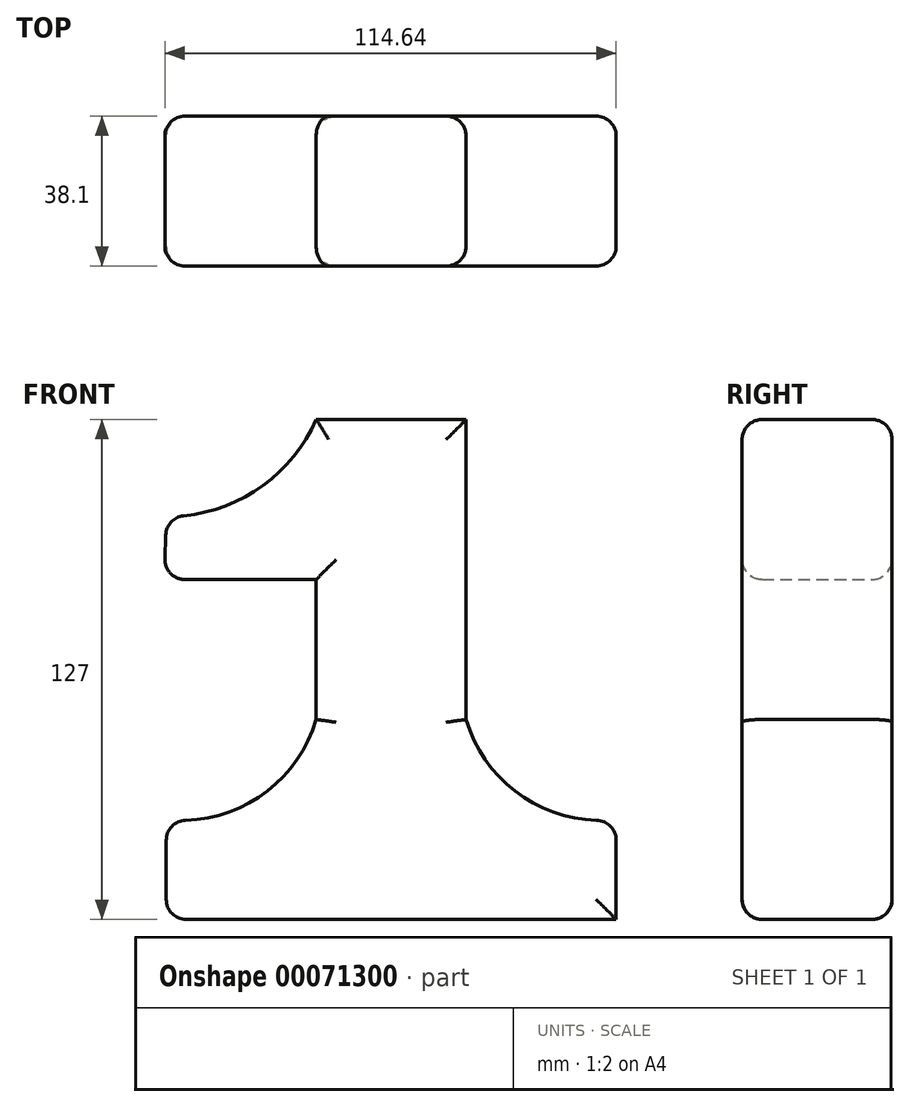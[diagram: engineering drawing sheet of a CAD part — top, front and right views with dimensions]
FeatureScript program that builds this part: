
annotation { "Feature Type Name" : "Feature", "Feature Type Description" : "" }
export const myFeature = defineFeature(function(context is Context, id is Id, definition is map)
    precondition{}
    {
        {
            var Q0;
            Q0=qCreatedBy(makeId("Front.planeOp"),FACE);
            var sketch = newSketch(context, id + "F0", { "sketchPlane" : qUnion([Q0])});
            skLineSegment(sketch, "E0.rect.bottom", {"start": v(19.05, -63.5) * mm, "end": v(-19.05, -63.5) * mm});
            skLineSegment(sketch, "E0.rect.top", {"start": v(19.05, 63.5) * mm, "end": v(-19.05, 63.5) * mm});
            skLineSegment(sketch, "E0.rect.left", {"start": v(19.05, -63.5) * mm, "end": v(19.05, 63.5) * mm});
            skLineSegment(sketch, "E0.rect.right", {"start": v(-19.05, -63.5) * mm, "end": v(-19.05, 63.5) * mm});
            skPoint(sketch, "E0.rect.middle", {"position": v(0, 0) * mm});
            skPoint(sketch, "E1", {"position": v(0, -63.5) * mm});
            skLineSegment(sketch, "E2", {"start": v(19.05, -63.5) * mm, "end": v(57.15, -63.5) * mm});
            skLineSegment(sketch, "E3", {"start": v(-19.05, -63.5) * mm, "end": v(-57.15, -63.5) * mm});
            skLineSegment(sketch, "E4", {"start": v(-57.15, -63.5) * mm, "end": v(-57.15, -38.1) * mm});
            skLineSegment(sketch, "E5", {"start": v(57.15, -63.5) * mm, "end": v(57.15, -38.1) * mm});
            skArc(sketch, "E6", {"start": v(-57.15, -38.1) * mm, "mid": v(-33.47, -32.35) * mm, "end": v(-19.05, -12.7) * mm});
            skArc(sketch, "E7", {"start": v(19.05, -12.7) * mm, "mid": v(33.47, -32.35) * mm, "end": v(57.15, -38.1) * mm});
            skArc(sketch, "E8", {"start": v(-57.15, 38.82) * mm, "mid": v(-34.41, 45.47) * mm, "end": v(-19.05, 63.5) * mm});
            skLineSegment(sketch, "E9", {"start": v(-19.05, 22.86) * mm, "end": v(-57.65, 22.86) * mm});
            skLineSegment(sketch, "E10", {"start": v(-57.65, 22.86) * mm, "end": v(-57.15, 38.82) * mm});
            skSolve(sketch);
        }
        {
            var Q0;
            {var subQ3=sQuery(id+"F0.wireOp",EDGE,"E0.rect.bottom");Q0=makeQuery(id+"F0.imprint","IMPRINT",FACE,{"disambiguationData":[TD([[makeQuery(id+"F0.imprint","IMPRINT",EDGE,{"derivedFrom":subQ3}),-1.0]])]});}
            var Q1;
            {var subQ0=sQuery(id+"F0.wireOp",EDGE,"E8");Q1=makeQuery(id+"F0.imprint","IMPRINT",FACE,{"disambiguationData":[TD([[makeQuery(id+"F0.imprint","IMPRINT",EDGE,{"derivedFrom":subQ0}),-1.0]])]});}
            var Q2;
            {var subQ0=sQuery(id+"F0.wireOp",EDGE,"E2");Q2=makeQuery(id+"F0.imprint","IMPRINT",FACE,{"disambiguationData":[TD([[makeQuery(id+"F0.imprint","IMPRINT",EDGE,{"derivedFrom":subQ0}),1.0]])]});}
            var Q3;
            {var subQ0=sQuery(id+"F0.wireOp",EDGE,"E3");Q3=makeQuery(id+"F0.imprint","IMPRINT",FACE,{"disambiguationData":[TD([[makeQuery(id+"F0.imprint","IMPRINT",EDGE,{"derivedFrom":subQ0}),-1.0]])]});}
            extrude(context, id + "F1", {"entities" : qUnion([Q0, Q1, Q2, Q3]), "endBound" : BoundingType.SYMMETRIC, "depth" : 38.1 * mm});
        }
        {
            var Q0;
            Q0=makeQuery(id+"F1.opExtrude","CAP_EDGE",EDGE,{"disambiguationData":[OSD([sQuery(id+"F0.wireOp",EDGE,"E0.rect.left")])],"isStart":false});
            var Q1;
            Q1=makeQuery(id+"F1.opExtrude","CAP_EDGE",EDGE,{"disambiguationData":[OSD([sQuery(id+"F0.wireOp",EDGE,"E7")])],"isStart":false});
            var Q2;
            Q2=makeQuery(id+"F1.opExtrude","CAP_EDGE",EDGE,{"disambiguationData":[OSD([sQuery(id+"F0.wireOp",EDGE,"E7")])],"isStart":true});
            var Q3;
            Q3=makeQuery(id+"F1.opExtrude","CAP_EDGE",EDGE,{"disambiguationData":[OSD([sQuery(id+"F0.wireOp",EDGE,"E0.rect.left")])],"isStart":true});
            var Q4;
            Q4=makeQuery(id+"F1.opExtrude","SWEPT_EDGE",EDGE,{"disambiguationData":[OSD([sQuery(id+"F0.wireOp",EDGE,"E5"),sQuery(id+"F0.wireOp",EDGE,"E7")])]});
            var Q5;
            Q5=makeQuery(id+"F1.opExtrude","CAP_EDGE",EDGE,{"disambiguationData":[OSD([sQuery(id+"F0.wireOp",EDGE,"E0.rect.top")])],"isStart":false});
            var Q6;
            Q6=makeQuery(id+"F1.opExtrude","CAP_EDGE",EDGE,{"disambiguationData":[OSD([sQuery(id+"F0.wireOp",EDGE,"E0.rect.top")])],"isStart":true});
            var Q7;
            Q7=makeQuery(id+"F1.opExtrude","CAP_EDGE",EDGE,{"disambiguationData":[OSD([sQuery(id+"F0.wireOp",EDGE,"E8")])],"isStart":false});
            var Q8;
            Q8=makeQuery(id+"F1.opExtrude","CAP_EDGE",EDGE,{"disambiguationData":[OSD([sQuery(id+"F0.wireOp",EDGE,"E8")])],"isStart":true});
            var Q9;
            Q9=makeQuery(id+"F1.opExtrude","CAP_EDGE",EDGE,{"disambiguationData":[OSD([sQuery(id+"F0.wireOp",EDGE,"E0.rect.right")])],"isStart":true});
            var Q10;
            Q10=makeQuery(id+"F1.opExtrude","CAP_EDGE",EDGE,{"disambiguationData":[OSD([sQuery(id+"F0.wireOp",EDGE,"E6")])],"isStart":true});
            var Q11;
            Q11=makeQuery(id+"F1.opExtrude","CAP_EDGE",EDGE,{"disambiguationData":[OSD([sQuery(id+"F0.wireOp",EDGE,"E9")])],"isStart":true});
            var Q12;
            Q12=makeQuery(id+"F1.opExtrude","CAP_EDGE",EDGE,{"disambiguationData":[OSD([sQuery(id+"F0.wireOp",EDGE,"E9")])],"isStart":false});
            var Q13;
            Q13=makeQuery(id+"F1.opExtrude","CAP_EDGE",EDGE,{"disambiguationData":[OSD([sQuery(id+"F0.wireOp",EDGE,"E0.rect.right")])],"isStart":false});
            var Q14;
            Q14=makeQuery(id+"F1.opExtrude","CAP_EDGE",EDGE,{"disambiguationData":[OSD([sQuery(id+"F0.wireOp",EDGE,"E6")])],"isStart":false});
            var Q15;
            Q15=makeQuery(id+"F1.opExtrude","CAP_EDGE",EDGE,{"disambiguationData":[OSD([sQuery(id+"F0.wireOp",EDGE,"E0.rect.bottom"),sQuery(id+"F0.wireOp",EDGE,"E2"),sQuery(id+"F0.wireOp",EDGE,"E3")])],"isStart":false});
            var Q16;
            Q16=makeQuery(id+"F1.opExtrude","CAP_EDGE",EDGE,{"disambiguationData":[OSD([sQuery(id+"F0.wireOp",EDGE,"E4")])],"isStart":false});
            var Q17;
            Q17=makeQuery(id+"F1.opExtrude","CAP_EDGE",EDGE,{"disambiguationData":[OSD([sQuery(id+"F0.wireOp",EDGE,"E5")])],"isStart":false});
            var Q18;
            Q18=makeQuery(id+"F1.opExtrude","CAP_EDGE",EDGE,{"disambiguationData":[OSD([sQuery(id+"F0.wireOp",EDGE,"E4")])],"isStart":true});
            var Q19;
            Q19=makeQuery(id+"F1.opExtrude","CAP_EDGE",EDGE,{"disambiguationData":[OSD([sQuery(id+"F0.wireOp",EDGE,"E0.rect.bottom"),sQuery(id+"F0.wireOp",EDGE,"E2"),sQuery(id+"F0.wireOp",EDGE,"E3")])],"isStart":true});
            var Q20;
            Q20=makeQuery(id+"F1.opExtrude","CAP_EDGE",EDGE,{"disambiguationData":[OSD([sQuery(id+"F0.wireOp",EDGE,"E5")])],"isStart":true});
            var Q21;
            Q21=makeQuery(id+"F1.opExtrude","SWEPT_EDGE",EDGE,{"disambiguationData":[OSD([sQuery(id+"F0.wireOp",EDGE,"E3"),sQuery(id+"F0.wireOp",EDGE,"E4")])]});
            var Q22;
            Q22=makeQuery(id+"F1.opExtrude","SWEPT_EDGE",EDGE,{"disambiguationData":[OSD([sQuery(id+"F0.wireOp",EDGE,"E4"),sQuery(id+"F0.wireOp",EDGE,"E6")])]});
            var Q23;
            Q23=makeQuery(id+"F1.opExtrude","SWEPT_FACE",FACE,{"disambiguationData":[OSD([sQuery(id+"F0.wireOp",EDGE,"E10")])]});
            fillet(context, id + "F2", {"entities" : qUnion([Q0, Q1, Q2, Q3, Q4, Q5, Q6, Q7, Q8, Q9, Q10, Q11, Q12, Q13, Q14, Q15, Q16, Q17, Q18, Q19, Q20, Q21, Q22, Q23]), "radius" : 5.08 * mm, "tangentPropagation" : true, "allowEdgeOverflow" : false});
        }
    });
